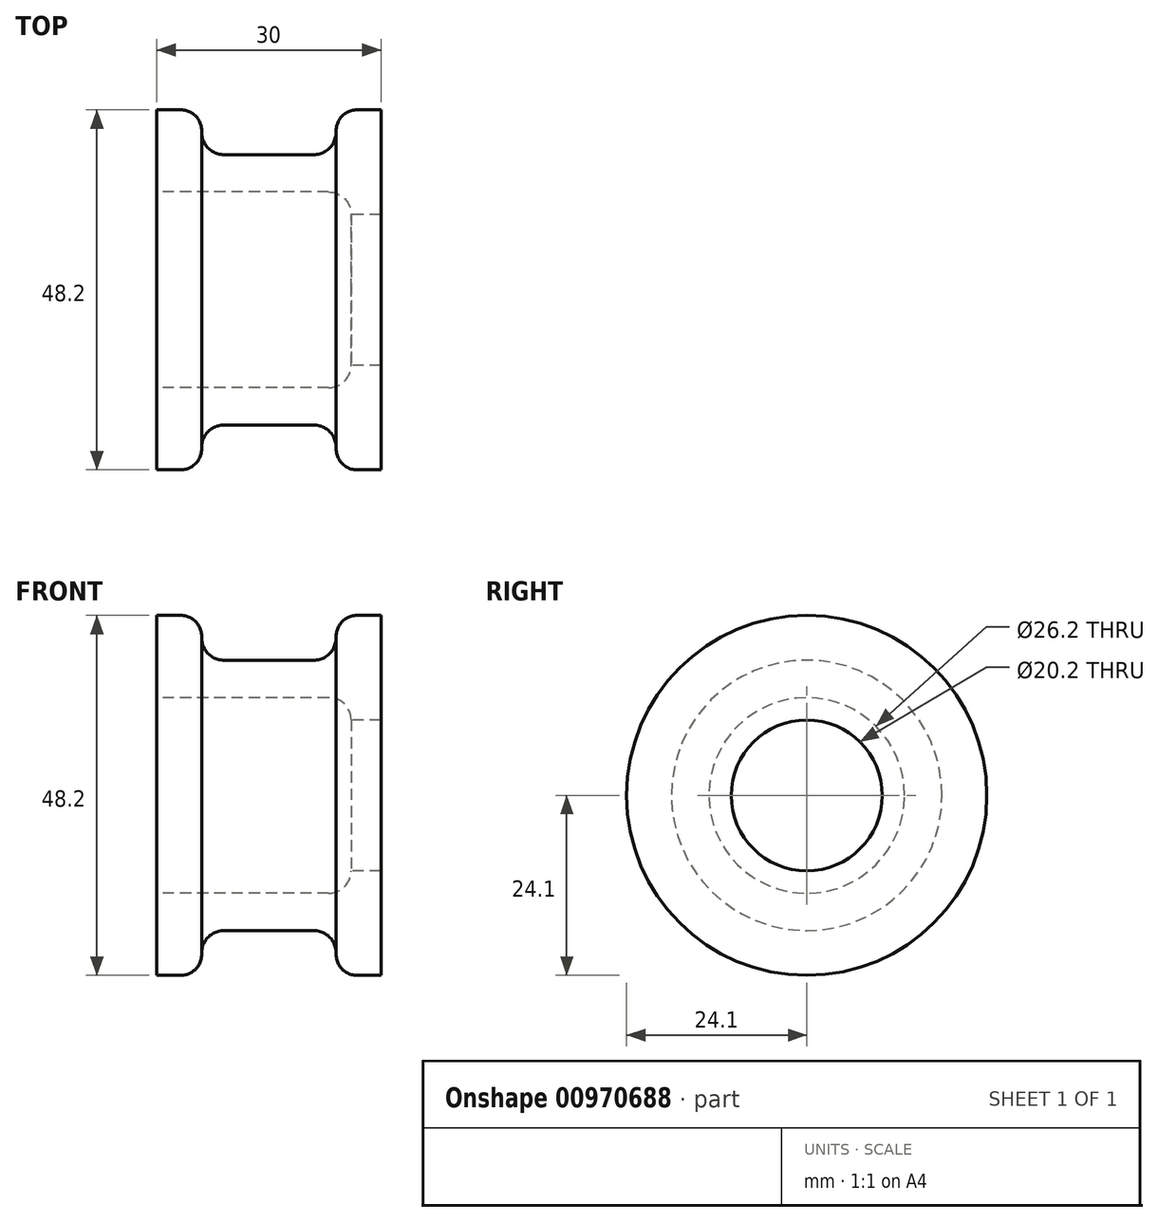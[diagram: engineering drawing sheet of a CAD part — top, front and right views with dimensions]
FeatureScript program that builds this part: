
annotation { "Feature Type Name" : "Feature", "Feature Type Description" : "" }
export const myFeature = defineFeature(function(context is Context, id is Id, definition is map)
    precondition{}
    {
        {
            var Q0;
            Q0=qCreatedBy(makeId("Front.planeOp"),FACE);
            var sketch = newSketch(context, id + "F0", { "sketchPlane" : qUnion([Q0])});
            skLineSegment(sketch, "E0", {"start": v(0, 13.1) * mm, "end": v(23, 13.1) * mm});
            skLineSegment(sketch, "E1", {"start": v(26, 10.1) * mm, "end": v(26, 10.1) * mm});
            skLineSegment(sketch, "E2", {"start": v(26, 10.1) * mm, "end": v(30, 10.1) * mm});
            skLineSegment(sketch, "E3", {"start": v(30, 10.1) * mm, "end": v(30, 24.1) * mm});
            skLineSegment(sketch, "E4", {"start": v(30, 24.1) * mm, "end": v(26.8, 24.1) * mm});
            skLineSegment(sketch, "E5", {"start": v(24, 21.3) * mm, "end": v(24, 21.1) * mm});
            skLineSegment(sketch, "E6", {"start": v(21, 18.1) * mm, "end": v(9, 18.1) * mm});
            skLineSegment(sketch, "E7", {"start": v(6, 21.1) * mm, "end": v(6, 21.3) * mm});
            skLineSegment(sketch, "E8", {"start": v(3.2, 24.1) * mm, "end": v(0, 24.1) * mm});
            skLineSegment(sketch, "E9", {"start": v(0, 24.1) * mm, "end": v(0, 13.08) * mm});
            skPoint(sketch, "E10.visualSharp", {"position": v(6, 18.1) * mm});
            skArc(sketch, "E10.filletArc", {"start": v(6, 21.1) * mm, "mid": v(6.88, 18.98) * mm, "end": v(9, 18.1) * mm});
            skPoint(sketch, "E11.visualSharp", {"position": v(24, 18.1) * mm});
            skArc(sketch, "E11.filletArc", {"start": v(21, 18.1) * mm, "mid": v(23.12, 18.98) * mm, "end": v(24, 21.1) * mm});
            skPoint(sketch, "E12.visualSharp", {"position": v(26, 13.1) * mm});
            skArc(sketch, "E12.filletArc", {"start": v(26, 10.1) * mm, "mid": v(25.12, 12.22) * mm, "end": v(23, 13.1) * mm});
            skLineSegment(sketch, "E13", {"start": v(0, 0) * mm, "end": v(47.84, 0) * mm, "construction": true});
            skPoint(sketch, "E14.visualSharp", {"position": v(6, 24.1) * mm});
            skArc(sketch, "E14.filletArc", {"start": v(6, 21.3) * mm, "mid": v(5.18, 23.28) * mm, "end": v(3.2, 24.1) * mm});
            skPoint(sketch, "E15.visualSharp", {"position": v(24, 24.1) * mm});
            skArc(sketch, "E15.filletArc", {"start": v(26.8, 24.1) * mm, "mid": v(24.82, 23.28) * mm, "end": v(24, 21.3) * mm});
            skSolve(sketch);
        }
        {
            var Q0;
            {var subQ1=sQuery(id+"F0.wireOp",EDGE,"E0");Q0=makeQuery(id+"F0.imprint","IMPRINT",FACE,{"disambiguationData":[TD([[makeQuery(id+"F0.imprint","IMPRINT",EDGE,{"derivedFrom":subQ1}),1.0]])]});}
            var Q1;
            Q1=sQuery(id+"F0.wireOp",EDGE,"E13");
            revolve(context, id + "F1", {"surfaceOperationType" : NewSurfaceOperationType.NEW, "entities" : qUnion([Q0]), "axis" : qUnion([Q1]), "revolveType" : RevolveType.FULL});
        }
    });
